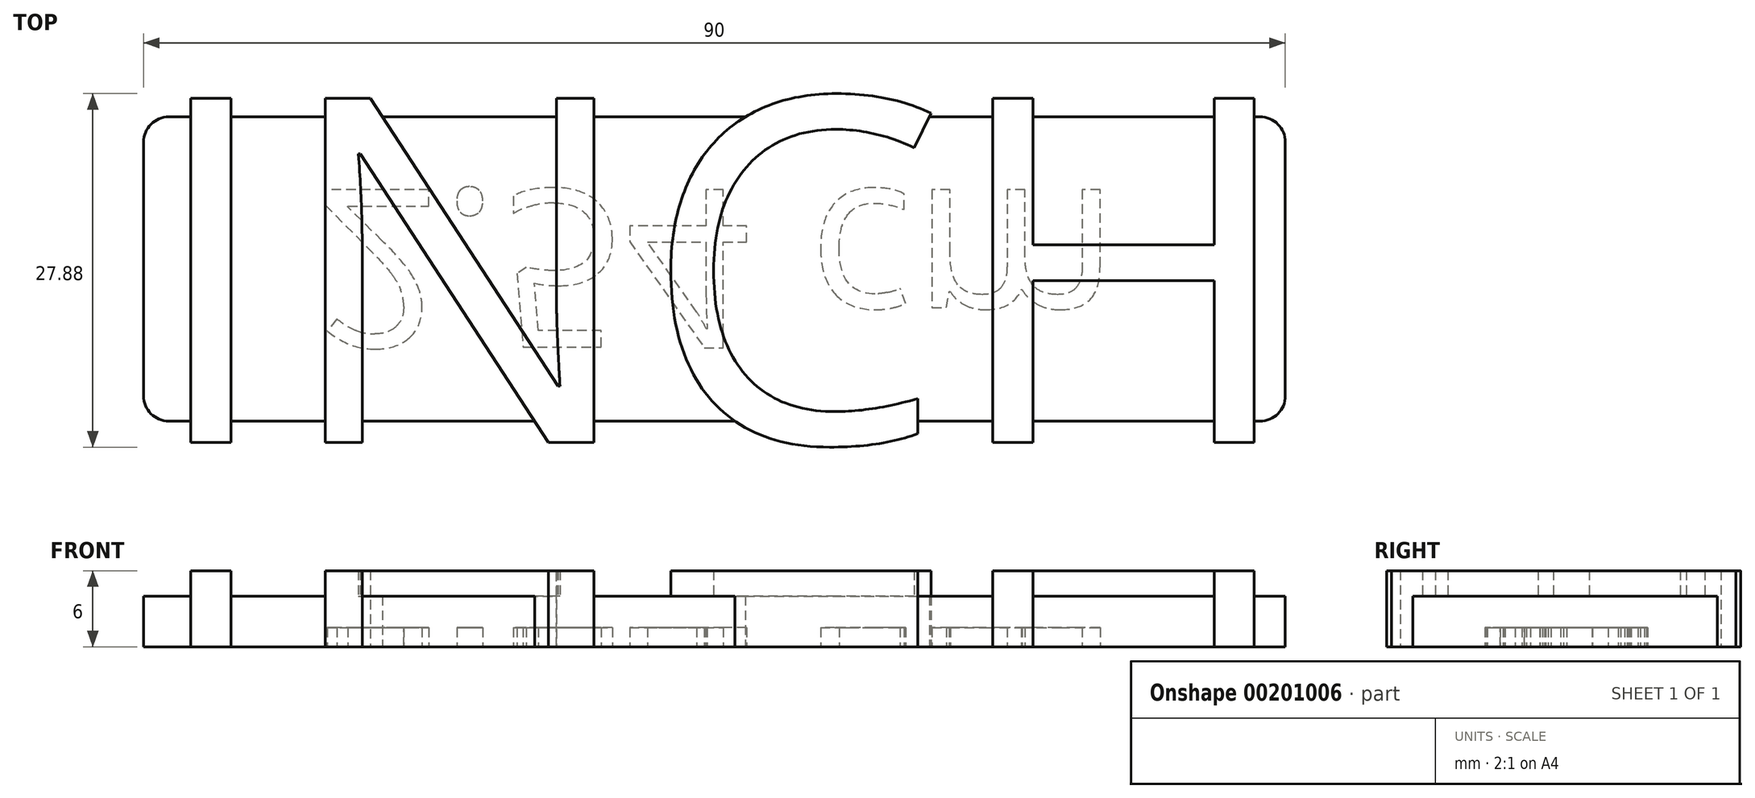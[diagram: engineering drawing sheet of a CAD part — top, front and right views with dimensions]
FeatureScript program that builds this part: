
annotation { "Feature Type Name" : "Feature", "Feature Type Description" : "" }
export const myFeature = defineFeature(function(context is Context, id is Id, definition is map)
    precondition{}
    {
        {
            var Q0;
            Q0=qCreatedBy(makeId("Top.planeOp"),FACE);
            var sketch = newSketch(context, id + "F0", { "sketchPlane" : qUnion([Q0])});
            skLineSegment(sketch, "E0.bottom", {"start": v(-45, 12) * mm, "end": v(45, 12) * mm});
            skLineSegment(sketch, "E0.top", {"start": v(-45, -12) * mm, "end": v(45, -12) * mm});
            skLineSegment(sketch, "E0.left", {"start": v(-45, 12) * mm, "end": v(-45, -12) * mm});
            skLineSegment(sketch, "E0.right", {"start": v(45, 12) * mm, "end": v(45, -12) * mm});
            skLineSegment(sketch, "E1", {"start": v(0, -12) * mm, "end": v(0, 12) * mm, "construction": true});
            skSolve(sketch);
        }
        {
            var Q0;
            Q0=makeQuery(id+"F0.imprint","IMPRINT",FACE,{"disambiguationData":[TD([[makeQuery(id+"F0.imprint","IMPRINT",EDGE,{"derivedFrom":sQuery(id+"F0.wireOp",EDGE,"E0.bottom")}),-1.0]])]});
            extrude(context, id + "F1", {"entities" : qUnion([Q0]), "depth" : 4 * mm});
        }
        {
            var Q0;
            Q0=makeQuery(id+"F1.opExtrude","SWEPT_EDGE",EDGE,{"disambiguationData":[OSD([sQuery(id+"F0.wireOp",EDGE,"E0.top"),sQuery(id+"F0.wireOp",EDGE,"E0.left")])]});
            var Q1;
            Q1=makeQuery(id+"F1.opExtrude","SWEPT_EDGE",EDGE,{"disambiguationData":[OSD([sQuery(id+"F0.wireOp",EDGE,"E0.bottom"),sQuery(id+"F0.wireOp",EDGE,"E0.right")])]});
            var Q2;
            Q2=makeQuery(id+"F1.opExtrude","SWEPT_EDGE",EDGE,{"disambiguationData":[OSD([sQuery(id+"F0.wireOp",EDGE,"E0.bottom"),sQuery(id+"F0.wireOp",EDGE,"E0.left")])]});
            var Q3;
            Q3=makeQuery(id+"F1.opExtrude","SWEPT_EDGE",EDGE,{"disambiguationData":[OSD([sQuery(id+"F0.wireOp",EDGE,"E0.top"),sQuery(id+"F0.wireOp",EDGE,"E0.right")])]});
            fillet(context, id + "F2", {"entities" : qUnion([Q0, Q1, Q2, Q3]), "radius" : 2 * mm, "tangentPropagation" : true, "allowEdgeOverflow" : false});
        }
        {
            var Q0;
            Q0=makeQuery(id+"F1.opExtrude","CAP_FACE",FACE,{"disambiguationData":[OSD([sQuery(id+"F0.wireOp",EDGE,"E0.bottom"),sQuery(id+"F0.wireOp",EDGE,"E0.top"),sQuery(id+"F0.wireOp",EDGE,"E0.left"),sQuery(id+"F0.wireOp",EDGE,"E0.right")])],"isStart":false});
            var sketch = newSketch(context, id + "F3", { "sketchPlane" : qUnion([Q0])});
            skText(sketch, "E2", { "text": "INCH", "fontName": "OpenSans-Regular.ttf"});
            const initialGuessF3  = {"E2": [-0.045, -0.01368, 1, 0, 0.02736]};
            skSetInitialGuess(sketch, initialGuessF3);
            skSolve(sketch);
        }
        {
            var Q0;
            {var subQ0=sQuery(id+"F3.wireOp",EDGE,"E2.sketch_text.stroke-4");Q0=makeQuery(id+"F3.imprint","IMPRINT",FACE,{"disambiguationData":[TD([[makeQuery(id+"F3.imprint","IMPRINT",EDGE,{"derivedFrom":subQ0}),-1.0]])]});}
            var Q1;
            {var subQ0=sQuery(id+"F3.wireOp",EDGE,"E2.sketch_text.stroke-3");var subQ1=sQuery(id+"F3.wireOp",EDGE,"E2.sketch_text.stroke-2");var subQ2=makeQuery(id+"F3.imprint","INTERSECT",VERTEX,{"derivedFrom":[subQ1,subQ0]});Q1=makeQuery(id+"F3.imprint","IMPRINT",FACE,{"disambiguationData":[TD([[makeQuery(id+"F3.imprint","IMPRINT",EDGE,{"disambiguationData":[TD([[subQ2,1.0]])],"derivedFrom":subQ1}),-1.0]])]});}
            var Q2;
            {var subQ1=sQuery(id+"F3.wireOp",EDGE,"E2.sketch_text.stroke-1");Q2=makeQuery(id+"F3.imprint","IMPRINT",FACE,{"disambiguationData":[TD([[makeQuery(id+"F3.imprint","IMPRINT",EDGE,{"derivedFrom":subQ1}),-1.0]])]});}
            var Q3;
            {var subQ0=sQuery(id+"F3.wireOp",EDGE,"E2.sketch_text.stroke-0");var subQ1=makeQuery(id+"F1.opExtrude","CAP_EDGE",EDGE,{"disambiguationData":[OSD([sQuery(id+"F0.wireOp",EDGE,"E0.top")])],"isStart":false});var subQ2=makeQuery(id+"F3.imprint","INTERSECT",VERTEX,{"derivedFrom":[subQ1,subQ0]});Q3=makeQuery(id+"F3.imprint","IMPRINT",FACE,{"disambiguationData":[TD([[makeQuery(id+"F3.imprint","IMPRINT",EDGE,{"disambiguationData":[TD([[subQ2,-1.0]])],"derivedFrom":subQ0}),-1.0]])]});}
            var Q4;
            {var subQ1=sQuery(id+"F3.wireOp",EDGE,"E2.sketch_text.stroke-8");Q4=makeQuery(id+"F3.imprint","IMPRINT",FACE,{"disambiguationData":[TD([[makeQuery(id+"F3.imprint","IMPRINT",EDGE,{"derivedFrom":subQ1}),-1.0]])]});}
            var Q5;
            {var subQ0=sQuery(id+"F3.wireOp",EDGE,"E2.sketch_text.stroke-9");var subQ1=makeQuery(id+"F1.opExtrude","CAP_EDGE",EDGE,{"disambiguationData":[OSD([sQuery(id+"F0.wireOp",EDGE,"E0.bottom")])],"isStart":false});var subQ2=makeQuery(id+"F3.imprint","INTERSECT",VERTEX,{"derivedFrom":[subQ1,subQ0]});Q5=makeQuery(id+"F3.imprint","IMPRINT",FACE,{"disambiguationData":[TD([[makeQuery(id+"F3.imprint","IMPRINT",EDGE,{"disambiguationData":[TD([[subQ2,1.0]])],"derivedFrom":subQ0}),-1.0]])]});}
            var Q6;
            {var subQ1=sQuery(id+"F3.wireOp",EDGE,"E2.sketch_text.stroke-10");Q6=makeQuery(id+"F3.imprint","IMPRINT",FACE,{"disambiguationData":[TD([[makeQuery(id+"F3.imprint","IMPRINT",EDGE,{"derivedFrom":subQ1}),-1.0]])]});}
            var Q7;
            {var subQ0=sQuery(id+"F3.wireOp",EDGE,"E2.sketch_text.stroke-11");var subQ1=makeQuery(id+"F1.opExtrude","CAP_EDGE",EDGE,{"disambiguationData":[OSD([sQuery(id+"F0.wireOp",EDGE,"E0.bottom")])],"isStart":false});var subQ2=makeQuery(id+"F3.imprint","INTERSECT",VERTEX,{"derivedFrom":[subQ1,subQ0]});Q7=makeQuery(id+"F3.imprint","IMPRINT",FACE,{"disambiguationData":[TD([[makeQuery(id+"F3.imprint","IMPRINT",EDGE,{"disambiguationData":[TD([[subQ2,-1.0]])],"derivedFrom":subQ0}),-1.0]])]});}
            var Q8;
            {var subQ0=sQuery(id+"F3.wireOp",EDGE,"E2.sketch_text.stroke-12");Q8=makeQuery(id+"F3.imprint","IMPRINT",FACE,{"disambiguationData":[TD([[makeQuery(id+"F3.imprint","IMPRINT",EDGE,{"derivedFrom":subQ0}),-1.0]])]});}
            var Q9;
            {var subQ0=sQuery(id+"F3.wireOp",EDGE,"E2.sketch_text.stroke-21");Q9=makeQuery(id+"F3.imprint","IMPRINT",FACE,{"disambiguationData":[TD([[makeQuery(id+"F3.imprint","IMPRINT",EDGE,{"derivedFrom":subQ0}),-1.0]])]});}
            var Q10;
            {var subQ0=sQuery(id+"F3.wireOp",EDGE,"E2.sketch_text.stroke-18");var subQ1=makeQuery(id+"F1.opExtrude","CAP_EDGE",EDGE,{"disambiguationData":[OSD([sQuery(id+"F0.wireOp",EDGE,"E0.top")])],"isStart":false});var subQ2=makeQuery(id+"F3.imprint","INTERSECT",VERTEX,{"derivedFrom":[subQ1,subQ0]});Q10=makeQuery(id+"F3.imprint","IMPRINT",FACE,{"disambiguationData":[TD([[makeQuery(id+"F3.imprint","IMPRINT",EDGE,{"disambiguationData":[TD([[subQ2,-1.0]])],"derivedFrom":subQ0}),-1.0]])]});}
            var Q11;
            {var subQ0=sQuery(id+"F3.wireOp",EDGE,"E2.sketch_text.stroke-19");Q11=makeQuery(id+"F3.imprint","IMPRINT",FACE,{"disambiguationData":[TD([[makeQuery(id+"F3.imprint","IMPRINT",EDGE,{"derivedFrom":subQ0}),-1.0]])]});}
            var Q12;
            {var subQ0=sQuery(id+"F3.wireOp",EDGE,"E2.sketch_text.stroke-25");Q12=makeQuery(id+"F3.imprint","IMPRINT",FACE,{"disambiguationData":[TD([[makeQuery(id+"F3.imprint","IMPRINT",EDGE,{"derivedFrom":subQ0}),-1.0]])]});}
            var Q13;
            {var subQ0=sQuery(id+"F3.wireOp",EDGE,"E2.sketch_text.stroke-22");var subQ1=makeQuery(id+"F1.opExtrude","CAP_EDGE",EDGE,{"disambiguationData":[OSD([sQuery(id+"F0.wireOp",EDGE,"E0.top")])],"isStart":false});var subQ2=makeQuery(id+"F3.imprint","INTERSECT",VERTEX,{"derivedFrom":[subQ1,subQ0]});Q13=makeQuery(id+"F3.imprint","IMPRINT",FACE,{"disambiguationData":[TD([[makeQuery(id+"F3.imprint","IMPRINT",EDGE,{"disambiguationData":[TD([[subQ2,-1.0]])],"derivedFrom":subQ0}),-1.0]])]});}
            var Q14;
            {var subQ0=sQuery(id+"F3.wireOp",EDGE,"E2.sketch_text.stroke-23");Q14=makeQuery(id+"F3.imprint","IMPRINT",FACE,{"disambiguationData":[TD([[makeQuery(id+"F3.imprint","IMPRINT",EDGE,{"derivedFrom":subQ0}),-1.0]])]});}
            var Q15;
            {var subQ5=sQuery(id+"F3.wireOp",EDGE,"E2.sketch_text.stroke-28");Q15=makeQuery(id+"F3.imprint","IMPRINT",FACE,{"disambiguationData":[TD([[makeQuery(id+"F3.imprint","IMPRINT",EDGE,{"derivedFrom":subQ5}),-1.0]])]});}
            var Q16;
            {var subQ0=sQuery(id+"F3.wireOp",EDGE,"E2.sketch_text.stroke-34");Q16=makeQuery(id+"F3.imprint","IMPRINT",FACE,{"disambiguationData":[TD([[makeQuery(id+"F3.imprint","IMPRINT",EDGE,{"derivedFrom":subQ0}),-1.0]])]});}
            var Q17;
            {var subQ0=sQuery(id+"F3.wireOp",EDGE,"E2.sketch_text.stroke-30");Q17=makeQuery(id+"F3.imprint","IMPRINT",FACE,{"disambiguationData":[TD([[makeQuery(id+"F3.imprint","IMPRINT",EDGE,{"derivedFrom":subQ0}),-1.0]])]});}
            var Q18;
            {var subQ0=sQuery(id+"F3.wireOp",EDGE,"E2.sketch_text.stroke-6");Q18=makeQuery(id+"F3.imprint","IMPRINT",FACE,{"disambiguationData":[TD([[makeQuery(id+"F3.imprint","IMPRINT",EDGE,{"derivedFrom":subQ0}),-1.0]])]});}
            var Q19;
            {var subQ0=sQuery(id+"F3.wireOp",EDGE,"E2.sketch_text.stroke-17");Q19=makeQuery(id+"F3.imprint","IMPRINT",FACE,{"disambiguationData":[TD([[makeQuery(id+"F3.imprint","IMPRINT",EDGE,{"derivedFrom":subQ0}),-1.0]])]});}
            var Q20;
            {var subQ0=sQuery(id+"F3.wireOp",EDGE,"E2.sketch_text.stroke-27");Q20=makeQuery(id+"F3.imprint","IMPRINT",FACE,{"disambiguationData":[TD([[makeQuery(id+"F3.imprint","IMPRINT",EDGE,{"derivedFrom":subQ0}),-1.0]])]});}
            var Q21;
            {var subQ0=sQuery(id+"F3.wireOp",EDGE,"E2.sketch_text.stroke-38");Q21=makeQuery(id+"F3.imprint","IMPRINT",FACE,{"disambiguationData":[TD([[makeQuery(id+"F3.imprint","IMPRINT",EDGE,{"derivedFrom":subQ0}),-1.0]])]});}
            var Q22;
            {var subQ5=sQuery(id+"F3.wireOp",EDGE,"E2.sketch_text.stroke-36");Q22=makeQuery(id+"F3.imprint","IMPRINT",FACE,{"disambiguationData":[TD([[makeQuery(id+"F3.imprint","IMPRINT",EDGE,{"derivedFrom":subQ5}),-1.0]])]});}
            var Q23;
            {var subQ0=sQuery(id+"F3.wireOp",EDGE,"E2.sketch_text.stroke-44");Q23=makeQuery(id+"F3.imprint","IMPRINT",FACE,{"disambiguationData":[TD([[makeQuery(id+"F3.imprint","IMPRINT",EDGE,{"derivedFrom":subQ0}),-1.0]])]});}
            var Q24;
            {var subQ0=sQuery(id+"F3.wireOp",EDGE,"E2.sketch_text.stroke-40");Q24=makeQuery(id+"F3.imprint","IMPRINT",FACE,{"disambiguationData":[TD([[makeQuery(id+"F3.imprint","IMPRINT",EDGE,{"derivedFrom":subQ0}),-1.0]])]});}
            extrude(context, id + "F4", {"entities" : qUnion([Q0, Q1, Q2, Q3, Q4, Q5, Q6, Q7, Q8, Q9, Q10, Q11, Q12, Q13, Q14, Q15, Q16, Q17, Q18, Q19, Q20, Q21, Q22, Q23, Q24]), "operationType" : NewBodyOperationType.ADD, "depth" : 2 * mm, "hasSecondDirection" : true, "secondDirectionOppositeDirection" : true, "secondDirectionDepth" : 4 * mm});
        }
        {
            var Q0;
            Q0=makeQuery(id+"F1.opExtrude","CAP_FACE",FACE,{"disambiguationData":[OSD([sQuery(id+"F0.wireOp",EDGE,"E0.bottom"),sQuery(id+"F0.wireOp",EDGE,"E0.top"),sQuery(id+"F0.wireOp",EDGE,"E0.left"),sQuery(id+"F0.wireOp",EDGE,"E0.right")])],"isStart":true});
            var sketch = newSketch(context, id + "F5", { "sketchPlane" : qUnion([Q0])});
            skText(sketch, "E3", { "text": "2.54 cm", "fontName": "OpenSans-Regular.ttf"});
            const initialGuessF5  = {"E3": [-0.03152, -0.00625, 1, 0, 0.0125]};
            skSetInitialGuess(sketch, initialGuessF5);
            skSolve(sketch);
        }
        {
            var Q0;
            Q0=makeQuery(id+"F5.imprint","IMPRINT",FACE,{"disambiguationData":[TD([[makeQuery(id+"F5.imprint","IMPRINT",EDGE,{"derivedFrom":sQuery(id+"F5.wireOp",EDGE,"E3.sketch_text.stroke-103")}),-1.0]])]});
            var Q1;
            Q1=makeQuery(id+"F5.imprint","IMPRINT",FACE,{"disambiguationData":[TD([[makeQuery(id+"F5.imprint","IMPRINT",EDGE,{"derivedFrom":sQuery(id+"F5.wireOp",EDGE,"E3.sketch_text.stroke-86")}),-1.0]])]});
            var Q2;
            Q2=makeQuery(id+"F5.imprint","IMPRINT",FACE,{"disambiguationData":[TD([[makeQuery(id+"F5.imprint","IMPRINT",EDGE,{"derivedFrom":sQuery(id+"F5.wireOp",EDGE,"E3.sketch_text.stroke-70")}),-1.0]])]});
            var Q3;
            Q3=makeQuery(id+"F5.imprint","IMPRINT",FACE,{"disambiguationData":[TD([[makeQuery(id+"F5.imprint","IMPRINT",EDGE,{"derivedFrom":sQuery(id+"F5.wireOp",EDGE,"E3.sketch_text.stroke-39")}),-1.0]])]});
            var Q4;
            Q4=makeQuery(id+"F5.imprint","IMPRINT",FACE,{"disambiguationData":[TD([[makeQuery(id+"F5.imprint","IMPRINT",EDGE,{"derivedFrom":sQuery(id+"F5.wireOp",EDGE,"E3.sketch_text.stroke-19")}),-1.0]])]});
            var Q5;
            Q5=makeQuery(id+"F5.imprint","IMPRINT",FACE,{"disambiguationData":[TD([[makeQuery(id+"F5.imprint","IMPRINT",EDGE,{"derivedFrom":sQuery(id+"F5.wireOp",EDGE,"E3.sketch_text.stroke-0")}),-1.0]])]});
            var Q6;
            Q6=makeQuery(id+"F5.imprint","IMPRINT",FACE,{"disambiguationData":[TD([[makeQuery(id+"F5.imprint","IMPRINT",EDGE,{"derivedFrom":sQuery(id+"F5.wireOp",EDGE,"E3.sketch_text.stroke-47")}),-1.0]])]});
            var Q7;
            Q7=makeQuery(id+"F5.imprint","IMPRINT",FACE,{"disambiguationData":[TD([[makeQuery(id+"F5.imprint","IMPRINT",EDGE,{"derivedFrom":sQuery(id+"F5.wireOp",EDGE,"E3.sketch_text.stroke-20")}),-1.0]])]});
            extrude(context, id + "F6", {"entities" : qUnion([Q0, Q1, Q2, Q3, Q4, Q5, Q6, Q7]), "operationType" : NewBodyOperationType.REMOVE, "oppositeDirection" : true, "depth" : 1.5 * mm});
        }
    });
